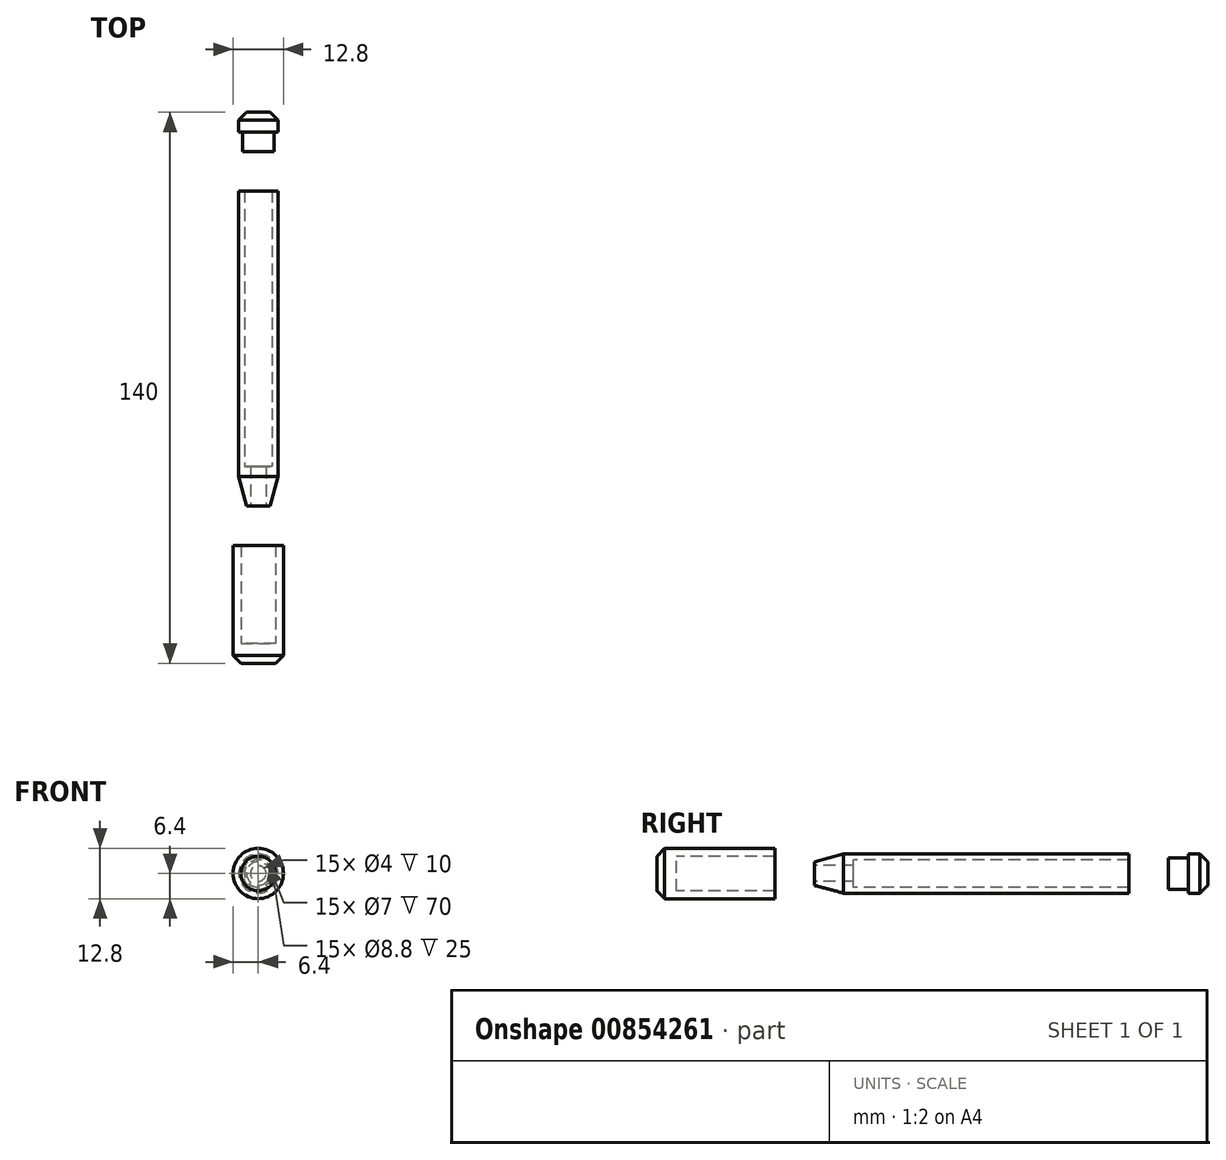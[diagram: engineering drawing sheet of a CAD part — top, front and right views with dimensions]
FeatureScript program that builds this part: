
annotation { "Feature Type Name" : "Feature", "Feature Type Description" : "" }
export const myFeature = defineFeature(function(context is Context, id is Id, definition is map)
    precondition{}
    {
        {
            var Q0;
            Q0=qCreatedBy(makeId("Right.planeOp"),FACE);
            var sketch = newSketch(context, id + "F0", { "sketchPlane" : qUnion([Q0])});
            skLineSegment(sketch, "E0", {"start": v(-72.54, 5) * mm, "end": v(0, 5) * mm});
            skLineSegment(sketch, "E1", {"start": v(0, 5) * mm, "end": v(0, 3.5) * mm});
            skLineSegment(sketch, "E2", {"start": v(-115, 4.4) * mm, "end": v(-115, 0) * mm});
            skLineSegment(sketch, "E3", {"start": v(-115, 0) * mm, "end": v(-120, 0) * mm});
            skLineSegment(sketch, "E4", {"start": v(-120, 0) * mm, "end": v(-120, 4.4) * mm});
            skLineSegment(sketch, "E5", {"start": v(-118, 6.4) * mm, "end": v(-90, 6.4) * mm});
            skLineSegment(sketch, "E6", {"start": v(-90, 4.4) * mm, "end": v(-90, 6.4) * mm});
            skLineSegment(sketch, "E7", {"start": v(-90, 4.4) * mm, "end": v(-115, 4.4) * mm});
            skLineSegment(sketch, "E8", {"start": v(-72.54, 5) * mm, "end": v(-80, 3) * mm});
            skLineSegment(sketch, "E9", {"start": v(-80, 3) * mm, "end": v(-80, 2) * mm});
            skLineSegment(sketch, "E10", {"start": v(15, 5) * mm, "end": v(15, 4) * mm});
            skLineSegment(sketch, "E11", {"start": v(10, 0) * mm, "end": v(20, 0) * mm});
            skLineSegment(sketch, "E12", {"start": v(20, 0) * mm, "end": v(20, 3) * mm});
            skLineSegment(sketch, "E13", {"start": v(18, 5) * mm, "end": v(20, 3) * mm});
            skLineSegment(sketch, "E14", {"start": v(18, 5) * mm, "end": v(15, 5) * mm});
            skLineSegment(sketch, "E15", {"start": v(15, 4) * mm, "end": v(10, 4) * mm});
            skLineSegment(sketch, "E16", {"start": v(10, 4) * mm, "end": v(10, 0) * mm});
            skPoint(sketch, "E17.orphan", {"position": v(0, 0) * mm});
            skLineSegment(sketch, "E18", {"start": v(-80, 2) * mm, "end": v(-70, 2) * mm});
            skLineSegment(sketch, "E19", {"start": v(-70, 2) * mm, "end": v(-70, 3.5) * mm});
            skLineSegment(sketch, "E20", {"start": v(-70, 3.5) * mm, "end": v(0, 3.5) * mm});
            skLineSegment(sketch, "E21", {"start": v(-80, 0) * mm, "end": v(0, 0) * mm, "construction": true});
            skLineSegment(sketch, "E22", {"start": v(-118, 6.4) * mm, "end": v(-120, 4.4) * mm});
            skSolve(sketch);
        }
        {
            var Q0;
            Q0=makeQuery(id+"F0.imprint","IMPRINT",FACE,{"disambiguationData":[TD([[makeQuery(id+"F0.imprint","IMPRINT",EDGE,{"derivedFrom":sQuery(id+"F0.wireOp",EDGE,"E2")}),-1.0]])]});
            var Q1;
            Q1=makeQuery(id+"F0.imprint","IMPRINT",FACE,{"disambiguationData":[TD([[makeQuery(id+"F0.imprint","IMPRINT",EDGE,{"derivedFrom":sQuery(id+"F0.wireOp",EDGE,"E0")}),-1.0]])]});
            var Q2;
            Q2=makeQuery(id+"F0.imprint","IMPRINT",FACE,{"disambiguationData":[TD([[makeQuery(id+"F0.imprint","IMPRINT",EDGE,{"derivedFrom":sQuery(id+"F0.wireOp",EDGE,"E10")}),1.0]])]});
            var Q3;
            Q3=sQuery(id+"F0.wireOp",EDGE,"E21");
            revolve(context, id + "F1", {"surfaceOperationType" : NewSurfaceOperationType.NEW, "entities" : qUnion([Q0, Q1, Q2]), "axis" : qUnion([Q3]), "revolveType" : RevolveType.FULL});
        }
    });
